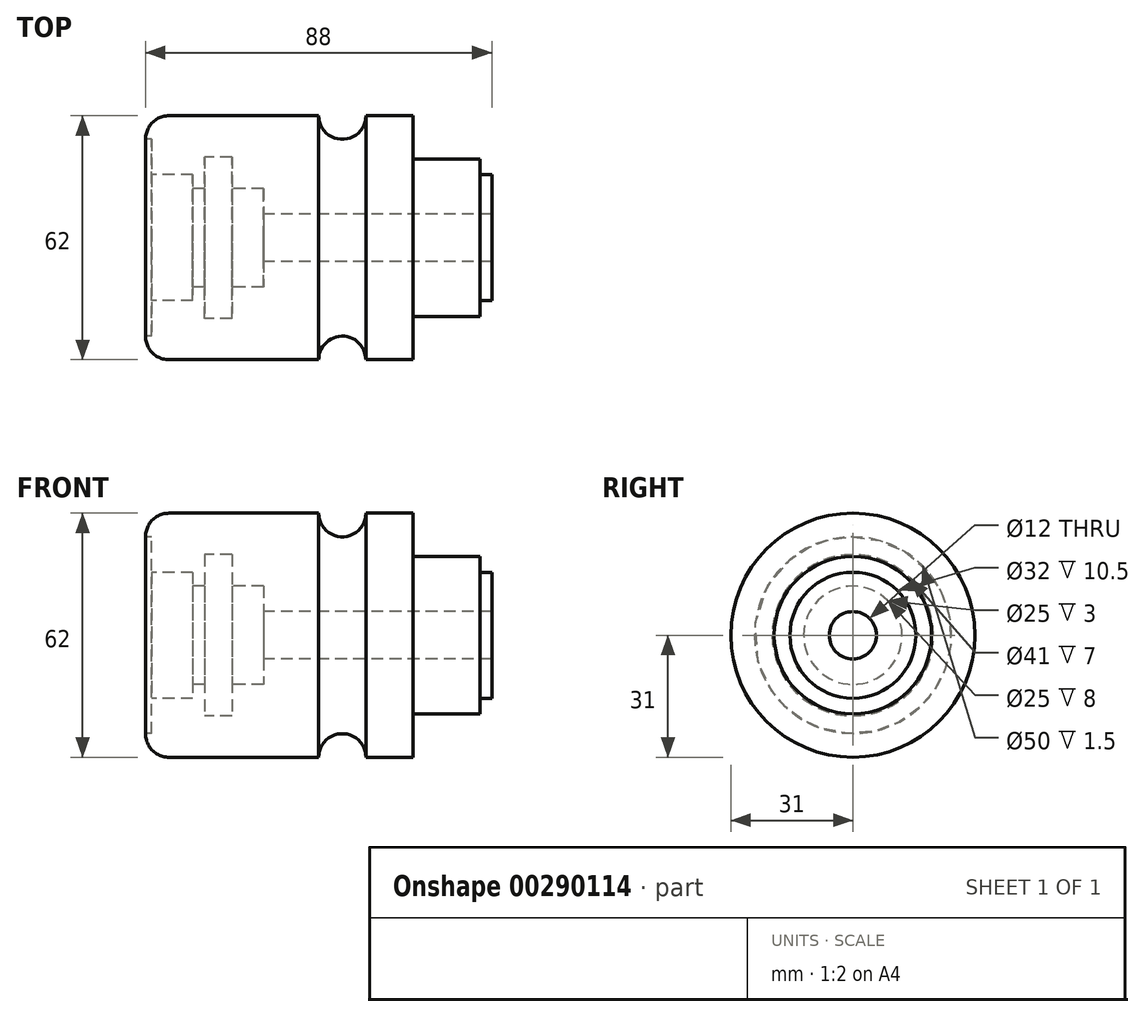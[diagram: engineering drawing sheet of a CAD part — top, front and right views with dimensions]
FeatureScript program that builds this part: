
annotation { "Feature Type Name" : "Feature", "Feature Type Description" : "" }
export const myFeature = defineFeature(function(context is Context, id is Id, definition is map)
    precondition{}
    {
        {
            var Q0;
            Q0=qCreatedBy(makeId("Front.planeOp"),FACE);
            var sketch = newSketch(context, id + "F0", { "sketchPlane" : qUnion([Q0])});
            skLineSegment(sketch, "E0", {"start": v(-44, 0) * mm, "end": v(44, 0) * mm, "construction": true});
            skLineSegment(sketch, "E1", {"start": v(32, 6) * mm, "end": v(32, 16) * mm});
            skLineSegment(sketch, "E2", {"start": v(32, 16) * mm, "end": v(29, 16) * mm});
            skLineSegment(sketch, "E3", {"start": v(29, 16) * mm, "end": v(29, 20) * mm});
            skLineSegment(sketch, "E4", {"start": v(29, 20) * mm, "end": v(12, 20) * mm});
            skLineSegment(sketch, "E5", {"start": v(12, 20) * mm, "end": v(12, 31) * mm});
            skLineSegment(sketch, "E6", {"start": v(12, 31) * mm, "end": v(0, 31) * mm});
            skArc(sketch, "E7", {"start": v(-12, 31) * mm, "mid": v(-6, 25) * mm, "end": v(0, 31) * mm});
            skLineSegment(sketch, "E8", {"start": v(-12, 31) * mm, "end": v(-56, 31) * mm});
            skLineSegment(sketch, "E9", {"start": v(32, 6) * mm, "end": v(-26, 6) * mm});
            skLineSegment(sketch, "E10", {"start": v(-26, 6) * mm, "end": v(-26, 12.5) * mm});
            skLineSegment(sketch, "E11", {"start": v(-26, 12.5) * mm, "end": v(-34, 12.5) * mm});
            skLineSegment(sketch, "E12", {"start": v(-34, 12.5) * mm, "end": v(-34, 20.5) * mm});
            skLineSegment(sketch, "E13", {"start": v(-34, 20.5) * mm, "end": v(-41, 20.5) * mm});
            skLineSegment(sketch, "E14", {"start": v(-41, 20.5) * mm, "end": v(-41, 12.5) * mm});
            skLineSegment(sketch, "E15", {"start": v(-41, 12.5) * mm, "end": v(-44, 12.5) * mm});
            skLineSegment(sketch, "E16", {"start": v(-44, 12.5) * mm, "end": v(-44, 16) * mm});
            skLineSegment(sketch, "E17", {"start": v(-44, 16) * mm, "end": v(-56, 16) * mm});
            skLineSegment(sketch, "E18", {"start": v(-56, 31) * mm, "end": v(-56, 16) * mm});
            skPoint(sketch, "E19", {"position": v(3, 6) * mm});
            skSolve(sketch);
        }
        {
            var Q0;
            Q0=makeQuery(id+"F0.imprint","IMPRINT",FACE,{"disambiguationData":[TD([[makeQuery(id+"F0.imprint","IMPRINT",EDGE,{"derivedFrom":sQuery(id+"F0.wireOp",EDGE,"E1")}),1.0]])]});
            var Q1;
            Q1=sQuery(id+"F0.wireOp",EDGE,"E0");
            revolve(context, id + "F1", {"entities" : qUnion([Q0]), "axis" : qUnion([Q1]), "revolveType" : RevolveType.FULL});
        }
        {
            var Q0;
            Q0=makeQuery(id+"F1.opRevolve","SWEPT_EDGE",EDGE,{"disambiguationData":[OSD([sQuery(id+"F0.wireOp",EDGE,"E8"),sQuery(id+"F0.wireOp",EDGE,"E18")])]});
            fillet(context, id + "F2", {"entities" : qUnion([Q0]), "radius" : 6 * mm, "tangentPropagation" : true, "allowEdgeOverflow" : false});
        }
        {
            var Q0;
            Q0=makeQuery(id+"F1.opRevolve","SWEPT_FACE",FACE,{"disambiguationData":[OSD([sQuery(id+"F0.wireOp",EDGE,"E18")])]});
            extrude(context, id + "F3", {"entities" : qUnion([Q0]), "operationType" : NewBodyOperationType.REMOVE, "oppositeDirection" : true, "depth" : 1.5 * mm});
        }
    });
